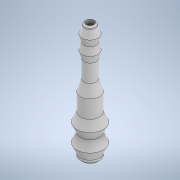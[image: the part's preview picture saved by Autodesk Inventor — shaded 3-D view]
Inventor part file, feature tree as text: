
AUTODESK INVENTOR PART (.ipt)
format: ipt  version: 2021 (Build 250183000, 183)  size: 157,696 bytes
history: native  units: in
note: dims shown in document units (in); Inventor stores cm internally (conversion verified against a paired STEP export)
features: revolve x1
ambient origin geometry x8: Origin, YZ Plane, XZ Plane, XY Plane, X Axis, Y Axis, Z Axis, Center Point
bodies: Solid1 (feature_tree)
feature tree (1):
  revolve  "Revolution1"  [1 undecoded]
note: 1 required parameter value undecoded (feature->parameter linkage not recoverable at this tier; creation-order binding heuristic only, values carry confidence <= 0.55)
